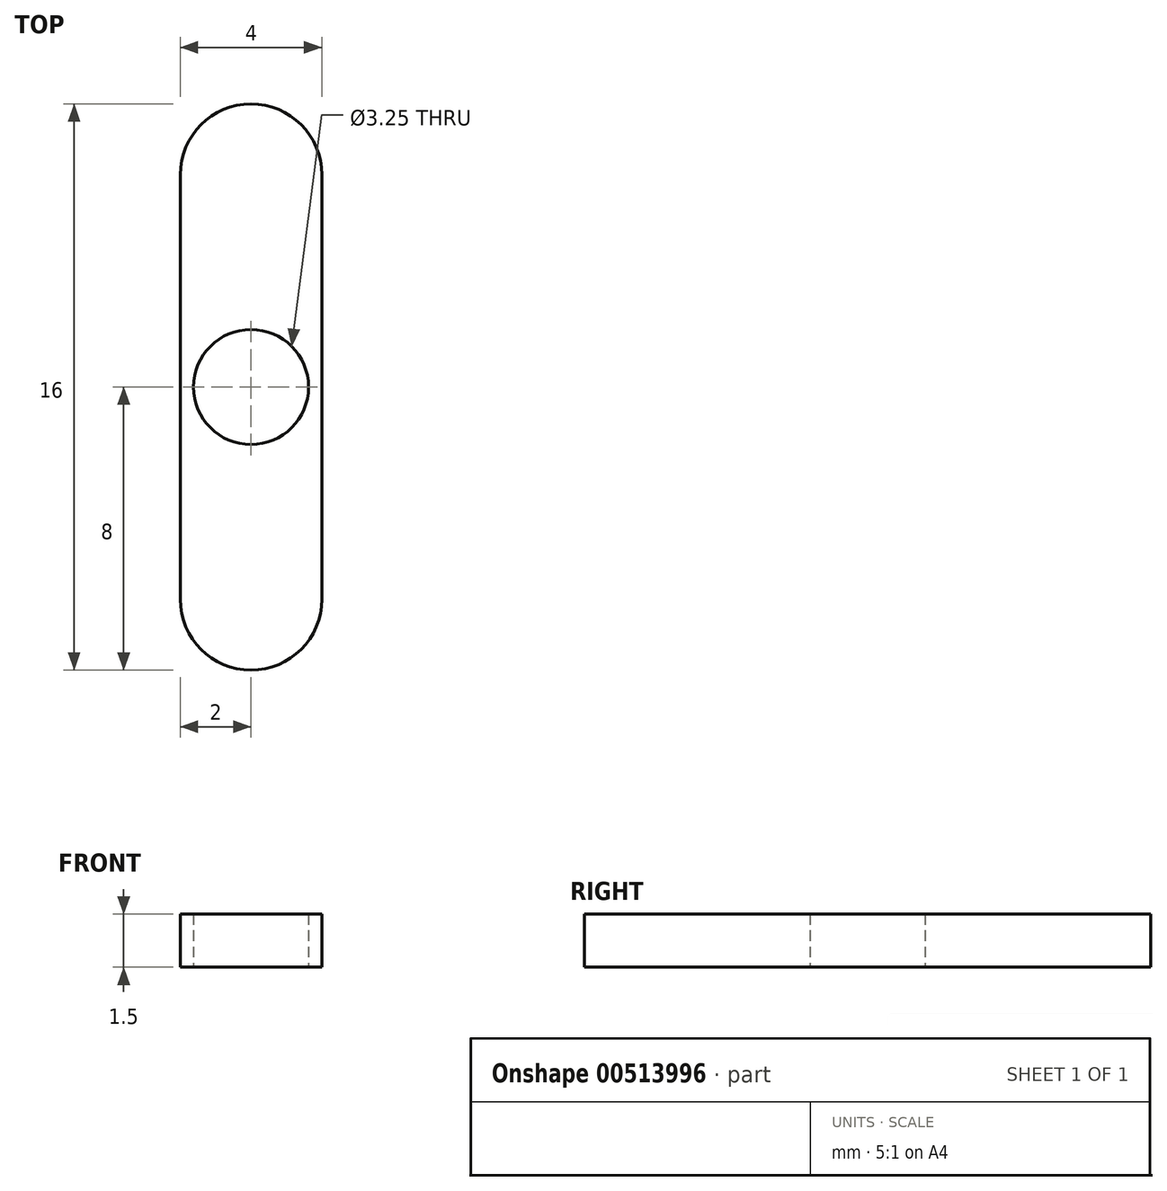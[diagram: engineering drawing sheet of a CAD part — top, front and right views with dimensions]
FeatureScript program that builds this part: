
annotation { "Feature Type Name" : "Feature", "Feature Type Description" : "" }
export const myFeature = defineFeature(function(context is Context, id is Id, definition is map)
    precondition{}
    {
        {
            var Q0;
            Q0=qCreatedBy(makeId("Top.planeOp"),FACE);
            var sketch = newSketch(context, id + "F0", { "sketchPlane" : qUnion([Q0])});
            skCircle(sketch, "E0", {"center": v(0, 0) * mm, "radius": 1.63 * mm});
            skCircle(sketch, "E1", {"center": v(0, 0) * mm, "radius": 2 * mm});
            skCircle(sketch, "E2", {"center": v(0, 6) * mm, "radius": 2 * mm});
            skLineSegment(sketch, "E3", {"start": v(-2, 6) * mm, "end": v(-2, 0) * mm});
            skLineSegment(sketch, "E4", {"start": v(2, 6) * mm, "end": v(2, 0) * mm});
            skCircle(sketch, "E5.2.0", {"center": v(0, -6) * mm, "radius": 2 * mm});
            skLineSegment(sketch, "E5.2.1", {"start": v(-2, -6) * mm, "end": v(-2, 0) * mm});
            skLineSegment(sketch, "E5.2.2", {"start": v(2, -6) * mm, "end": v(2, 0) * mm});
            skLineSegment(sketch, "E5.anchor1", {"start": v(0, 0) * mm, "end": v(0, 6) * mm, "construction": true});
            skLineSegment(sketch, "E5.anchor2", {"start": v(0, 0) * mm, "end": v(0, -6) * mm, "construction": true});
            skLineSegment(sketch, "E6", {"start": v(-4.42, 0) * mm, "end": v(5.76, 0) * mm});
            skSolve(sketch);
        }
        {
            var Q0;
            {var subQ0=sQuery(id+"F0.wireOp",EDGE,"E6");var subQ1=sQuery(id+"F0.wireOp",EDGE,"E0");var subQ2=makeQuery(id+"F0.imprint","INTERSECT",VERTEX,{"disambiguationData":[OD(0.0)],"derivedFrom":[subQ1,subQ0]});Q0=makeQuery(id+"F0.imprint","IMPRINT",FACE,{"disambiguationData":[TD([[makeQuery(id+"F0.imprint","IMPRINT",EDGE,{"disambiguationData":[TD([[subQ2,1.0]])],"derivedFrom":subQ1}),-1.0]])]});}
            var Q1;
            {var subQ0=sQuery(id+"F0.wireOp",EDGE,"E2");var subQ1=makeQuery(id+"F0.imprint","INTERSECT",VERTEX,{"derivedFrom":[subQ0,sQuery(id+"F0.wireOp",EDGE,"E3")]});Q1=makeQuery(id+"F0.imprint","IMPRINT",FACE,{"disambiguationData":[TD([[makeQuery(id+"F0.imprint","IMPRINT",EDGE,{"disambiguationData":[TD([[subQ1,1.0]])],"derivedFrom":subQ0}),1.0]])]});}
            var Q2;
            {var subQ1=sQuery(id+"F0.wireOp",EDGE,"E3");Q2=makeQuery(id+"F0.imprint","IMPRINT",FACE,{"disambiguationData":[TD([[makeQuery(id+"F0.imprint","IMPRINT",EDGE,{"derivedFrom":subQ1}),1.0]])]});}
            var Q3;
            {var subQ1=sQuery(id+"F0.wireOp",EDGE,"E5.2.1");Q3=makeQuery(id+"F0.imprint","IMPRINT",FACE,{"disambiguationData":[TD([[makeQuery(id+"F0.imprint","IMPRINT",EDGE,{"derivedFrom":subQ1}),-1.0]])]});}
            var Q4;
            {var subQ0=sQuery(id+"F0.wireOp",EDGE,"E5.2.0");var subQ1=makeQuery(id+"F0.imprint","INTERSECT",VERTEX,{"derivedFrom":[subQ0,sQuery(id+"F0.wireOp",EDGE,"E5.2.1")]});Q4=makeQuery(id+"F0.imprint","IMPRINT",FACE,{"disambiguationData":[TD([[makeQuery(id+"F0.imprint","IMPRINT",EDGE,{"disambiguationData":[TD([[subQ1,-1.0]])],"derivedFrom":subQ0}),1.0]])]});}
            var Q5;
            {var subQ0=sQuery(id+"F0.wireOp",EDGE,"E6");var subQ1=sQuery(id+"F0.wireOp",EDGE,"E0");var subQ2=makeQuery(id+"F0.imprint","INTERSECT",VERTEX,{"disambiguationData":[OD(0.0)],"derivedFrom":[subQ1,subQ0]});Q5=makeQuery(id+"F0.imprint","IMPRINT",FACE,{"disambiguationData":[TD([[makeQuery(id+"F0.imprint","IMPRINT",EDGE,{"disambiguationData":[TD([[subQ2,-1.0]])],"derivedFrom":subQ1}),-1.0]])]});}
            extrude(context, id + "F1", {"entities" : qUnion([Q0, Q1, Q2, Q3, Q4, Q5]), "depth" : 1.5 * mm});
        }
    });
